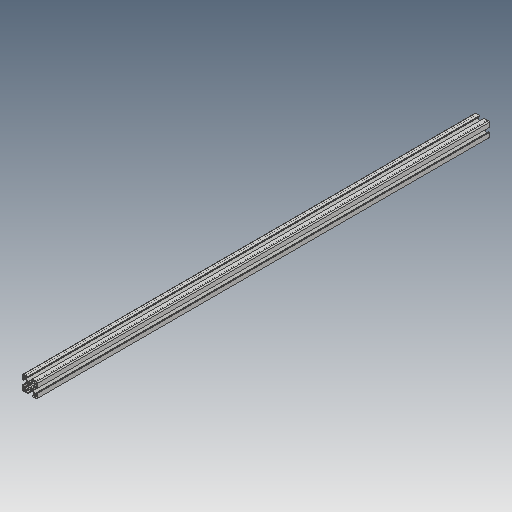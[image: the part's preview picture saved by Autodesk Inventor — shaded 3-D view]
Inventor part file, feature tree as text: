
AUTODESK INVENTOR PART (.ipt)
format: ipt  version: 2017 (Build 210142000, 142)  size: 275,456 bytes
history: native  units: mm
features: other x2, extrude x1, sketch x1, reference x1
ambient origin geometry x8: Origin, YZ Plane, XZ Plane, XY Plane, X Axis, Y Axis, Z Axis, Center Point
bodies: Solid1 (feature_tree)
feature tree (5):
  extrude  "Extrusion1"  [1 undecoded]
  sketch  "Sketch1"  dims[d0=900.0mm d1=0.0mm]
  reference  "Reference1"
  other  "<userpath>\OneDrive\Inventor\Beast 3D Printer\Assembly3.iam"
  other  "Assembly3.iam"
note: 1 required parameter value undecoded (feature->parameter linkage not recoverable at this tier; creation-order binding heuristic only, values carry confidence <= 0.55)
